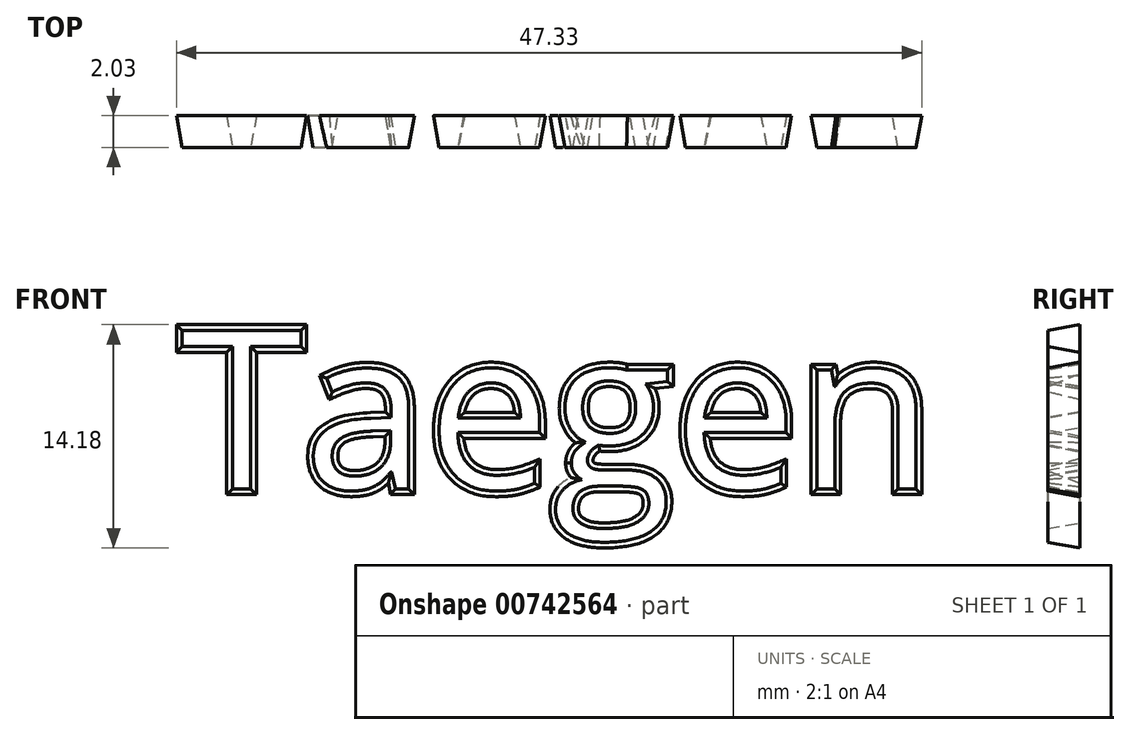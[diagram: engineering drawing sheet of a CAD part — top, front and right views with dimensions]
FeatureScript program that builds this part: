
annotation { "Feature Type Name" : "Feature", "Feature Type Description" : "" }
export const myFeature = defineFeature(function(context is Context, id is Id, definition is map)
    precondition{}
    {
        {
            var Q0;
            Q0=qCreatedBy(makeId("Front.planeOp"),FACE);
            var sketch = newSketch(context, id + "F0", { "sketchPlane" : qUnion([Q0])});
            skLineSegment(sketch, "E0.bottom", {"start": v(-25.4, 15.88) * mm, "end": v(25.4, 15.88) * mm});
            skLineSegment(sketch, "E0.top", {"start": v(-25.4, -15.88) * mm, "end": v(25.4, -15.88) * mm});
            skLineSegment(sketch, "E0.left", {"start": v(-25.4, 15.88) * mm, "end": v(-25.4, -15.88) * mm});
            skLineSegment(sketch, "E0.right", {"start": v(25.4, 15.87) * mm, "end": v(25.4, -15.88) * mm});
            skPoint(sketch, "E0.middle", {"position": v(0, 0) * mm});
            skSolve(sketch);
        }
        {
            var Q0;
            Q0=qCreatedBy(makeId("Front.planeOp"),FACE);
            var sketch = newSketch(context, id + "F1", { "sketchPlane" : qUnion([Q0])});
            skText(sketch, "E1", { "text": "Taegen", "fontName": "OpenSans-Regular.ttf"});
            const initialGuessF1  = {"E1": [-0.02383, -0.00508, 1, 0, 0.01016]};
            skSetInitialGuess(sketch, initialGuessF1);
            skSolve(sketch);
        }
        {
            var Q0;
            Q0=qSketchRegion(id+"F1",true);
            extrude(context, id + "F2", {"entities" : qUnion([Q0]), "oppositeDirection" : true, "depth" : 2.03 * mm, "offsetDistance" : 25.4 * mm, "hasDraft" : true, "draftAngle" : 10 * degree});
        }
    });
